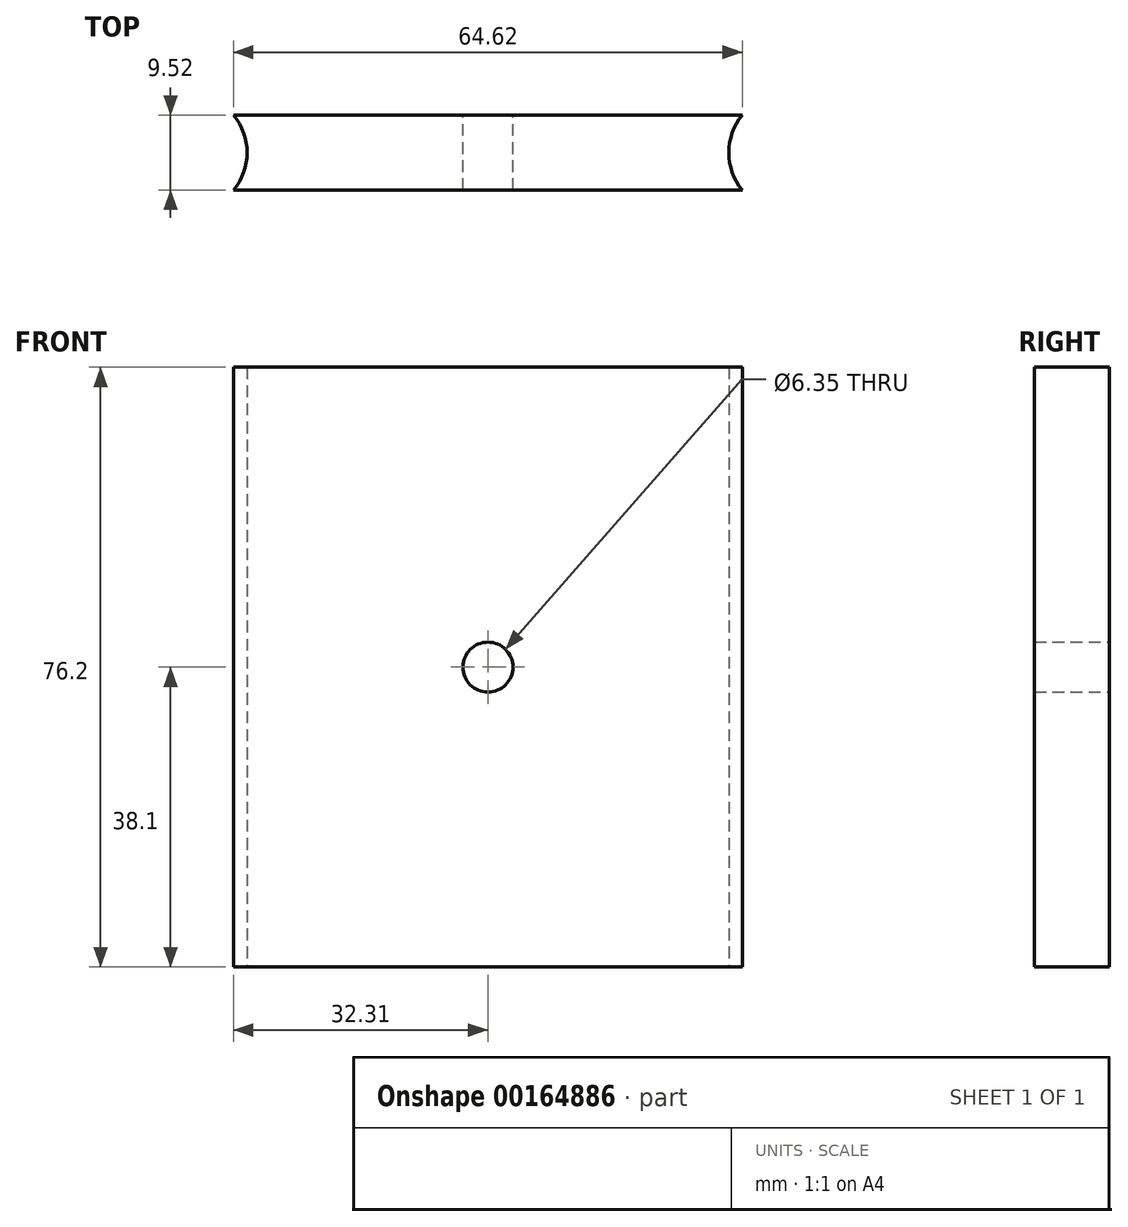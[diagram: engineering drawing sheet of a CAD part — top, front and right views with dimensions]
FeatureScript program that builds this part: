
annotation { "Feature Type Name" : "Feature", "Feature Type Description" : "" }
export const myFeature = defineFeature(function(context is Context, id is Id, definition is map)
    precondition{}
    {
        {
            var Q0;
            Q0=qCreatedBy(makeId("Top.planeOp"),FACE);
            var sketch = newSketch(context, id + "F0", { "sketchPlane" : qUnion([Q0])});
            skLineSegment(sketch, "E0.bottom", {"start": v(32.3, -4.76) * mm, "end": v(-32.3, -4.76) * mm});
            skLineSegment(sketch, "E0.top", {"start": v(32.3, 4.76) * mm, "end": v(-32.3, 4.76) * mm});
            skLineSegment(sketch, "E0.left", {"start": v(32.3, -4.76) * mm, "end": v(32.3, 4.76) * mm, "construction": true});
            skLineSegment(sketch, "E0.right", {"start": v(-32.3, -4.76) * mm, "end": v(-32.3, 4.76) * mm, "construction": true});
            skPoint(sketch, "E0.middle", {"position": v(0, 0) * mm});
            skArc(sketch, "E1", {"start": v(-32.3, -4.76) * mm, "mid": v(-30.6, 0) * mm, "end": v(-32.3, 4.76) * mm});
            skArc(sketch, "E2", {"start": v(32.3, 4.76) * mm, "mid": v(30.6, 0) * mm, "end": v(32.3, -4.76) * mm});
            skLineSegment(sketch, "E3", {"start": v(-38.1, 0) * mm, "end": v(38.1, 0) * mm, "construction": true});
            skSolve(sketch);
        }
        {
            var Q0;
            Q0=qSketchRegion(id+"F0",true);
            extrude(context, id + "F1", {"entities" : qUnion([Q0]), "depth" : 76.2 * mm});
        }
        {
            var Q0;
            Q0=makeQuery(id+"F1.opExtrude","SWEPT_FACE",FACE,{"disambiguationData":[OSD([sQuery(id+"F0.wireOp",EDGE,"E0.top")])]});
            var sketch = newSketch(context, id + "F2", { "sketchPlane" : qUnion([Q0])});
            skLineSegment(sketch, "E4", {"start": v(32.3, 38.1) * mm, "end": v(-32.3, 38.1) * mm, "construction": true});
            skCircle(sketch, "E5", {"center": v(0, 38.1) * mm, "radius": 3.18 * mm});
            skSolve(sketch);
        }
        {
            var Q0;
            Q0=qSketchRegion(id+"F2",true);
            var Q1;
            Q1=makeQuery(id+"F1.opExtrude","SWEPT_FACE",FACE,{"disambiguationData":[OSD([sQuery(id+"F0.wireOp",EDGE,"E0.bottom")])]});
            extrude(context, id + "F3", {"entities" : qUnion([Q0]), "operationType" : NewBodyOperationType.REMOVE, "endBound" : BoundingType.UP_TO_SURFACE, "oppositeDirection" : true, "endBoundEntityFace" : qUnion([Q1]), "depth" : 25.4 * mm});
        }
    });
